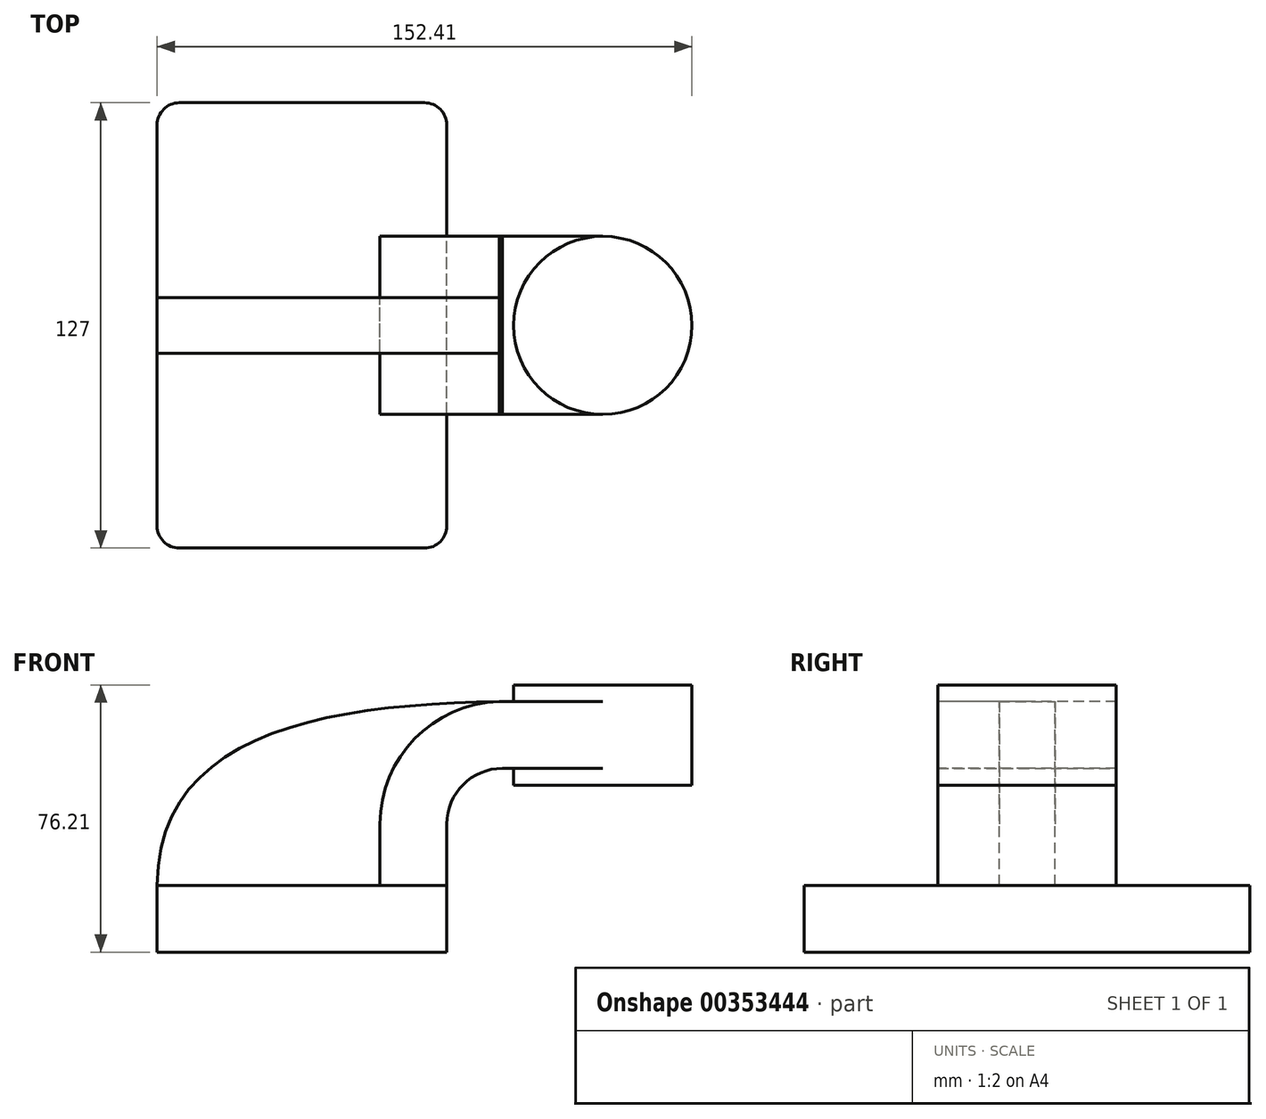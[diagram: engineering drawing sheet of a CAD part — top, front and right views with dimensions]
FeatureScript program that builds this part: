
annotation { "Feature Type Name" : "Feature", "Feature Type Description" : "" }
export const myFeature = defineFeature(function(context is Context, id is Id, definition is map)
    precondition{}
    {
        {
            var Q0;
            Q0=qCreatedBy(makeId("Front.planeOp"),FACE);
            var sketch = newSketch(context, id + "F0", { "sketchPlane" : qUnion([Q0])});
            skLineSegment(sketch, "E0.bottom", {"start": v(-41.28, -9.53) * mm, "end": v(41.28, -9.53) * mm});
            skLineSegment(sketch, "E0.top", {"start": v(-41.28, 9.53) * mm, "end": v(41.28, 9.53) * mm});
            skLineSegment(sketch, "E0.left", {"start": v(-41.28, -9.53) * mm, "end": v(-41.28, 9.53) * mm});
            skLineSegment(sketch, "E0.right", {"start": v(41.28, -9.53) * mm, "end": v(41.28, 9.53) * mm});
            skPoint(sketch, "E0.middle", {"position": v(0, 0) * mm});
            skLineSegment(sketch, "E1.bottom", {"start": v(60.33, 38.1) * mm, "end": v(111.12, 38.1) * mm});
            skLineSegment(sketch, "E1.top", {"start": v(60.33, 66.67) * mm, "end": v(111.12, 66.67) * mm});
            skLineSegment(sketch, "E1.left", {"start": v(60.33, 38.1) * mm, "end": v(60.33, 66.67) * mm});
            skLineSegment(sketch, "E1.right", {"start": v(111.12, 38.1) * mm, "end": v(111.12, 66.67) * mm});
            skPoint(sketch, "E1.middle", {"position": v(85.72, 52.39) * mm});
            skLineSegment(sketch, "E2", {"start": v(41.28, 9.53) * mm, "end": v(41.28, 27) * mm});
            skArc(sketch, "E3", {"start": v(41.27, 27) * mm, "mid": v(45.92, 38.23) * mm, "end": v(57.15, 42.88) * mm});
            skLineSegment(sketch, "E4", {"start": v(57.15, 42.88) * mm, "end": v(85.72, 42.88) * mm});
            skPoint(sketch, "E4.endSnap0", {"position": v(85.72, 38.1) * mm});
            skLineSegment(sketch, "E5.0", {"start": v(57.15, 61.93) * mm, "end": v(85.72, 61.93) * mm});
            skArc(sketch, "E5.1", {"start": v(22.23, 27) * mm, "mid": v(32.45, 51.7) * mm, "end": v(57.15, 61.93) * mm});
            skLineSegment(sketch, "E5.2", {"start": v(22.22, 9.53) * mm, "end": v(22.22, 27) * mm});
            skLineSegment(sketch, "E6", {"start": v(85.72, 38.1) * mm, "end": v(85.72, 66.67) * mm});
            skFitSpline(sketch, "E7", {"points": [v(-41.28, 9.53) * mm, v(57.15, 61.93) * mm], "startDerivative": vector(0.4, 131.51) * mm, "endDerivative": vector(149.24, 1.93) * mm});
            skSolve(sketch);
        }
        {
            var Q0;
            Q0=makeQuery(id+"F0.imprint","IMPRINT",FACE,{"disambiguationData":[TD([[makeQuery(id+"F0.imprint","IMPRINT",EDGE,{"derivedFrom":sQuery(id+"F0.wireOp",EDGE,"E0.bottom")}),1.0]])]});
            extrude(context, id + "F1", {"entities" : qUnion([Q0]), "endBound" : BoundingType.SYMMETRIC, "depth" : 127 * mm});
        }
        {
            var Q0;
            {var subQ1=sQuery(id+"F0.wireOp",EDGE,"E2");Q0=makeQuery(id+"F0.imprint","IMPRINT",FACE,{"disambiguationData":[TD([[makeQuery(id+"F0.imprint","IMPRINT",EDGE,{"derivedFrom":subQ1}),1.0]])]});}
            var Q1;
            {var subQ0=sQuery(id+"F0.wireOp",EDGE,"E4");var subQ1=sQuery(id+"F0.wireOp",EDGE,"E1.left");var subQ2=makeQuery(id+"F0.imprint","INTERSECT",VERTEX,{"derivedFrom":[subQ1,subQ0]});Q1=makeQuery(id+"F0.imprint","IMPRINT",FACE,{"disambiguationData":[TD([[makeQuery(id+"F0.imprint","IMPRINT",EDGE,{"disambiguationData":[TD([[subQ2,-1.0]])],"derivedFrom":subQ1}),-1.0]])]});}
            extrude(context, id + "F2", {"entities" : qUnion([Q0, Q1]), "endBound" : BoundingType.SYMMETRIC, "depth" : 50.8 * mm});
        }
        {
            var Q0;
            {var subQ3=sQuery(id+"F0.wireOp",EDGE,"E5.2");Q0=makeQuery(id+"F0.imprint","IMPRINT",FACE,{"disambiguationData":[TD([[makeQuery(id+"F0.imprint","IMPRINT",EDGE,{"derivedFrom":subQ3}),1.0]])]});}
            extrude(context, id + "F3", {"entities" : qUnion([Q0]), "endBound" : BoundingType.SYMMETRIC, "depth" : 15.88 * mm});
        }
        {
            var Q0;
            {var subQ4=sQuery(id+"F0.wireOp",EDGE,"E1.right");Q0=makeQuery(id+"F0.imprint","IMPRINT",FACE,{"disambiguationData":[TD([[makeQuery(id+"F0.imprint","IMPRINT",EDGE,{"derivedFrom":subQ4}),1.0]])]});}
            var Q1;
            Q1=sQuery(id+"F0.wireOp",EDGE,"E6");
            revolve(context, id + "F4", {"operationType" : NewBodyOperationType.ADD, "entities" : qUnion([Q0]), "axis" : qUnion([Q1]), "revolveType" : RevolveType.FULL});
        }
        {
            var Q0;
            Q0=makeQuery(id+"F1.opExtrude","CAP_EDGE",EDGE,{"disambiguationData":[OSD([sQuery(id+"F0.wireOp",EDGE,"E0.left")])],"isStart":false});
            var Q1;
            Q1=makeQuery(id+"F1.opExtrude","CAP_EDGE",EDGE,{"disambiguationData":[OSD([sQuery(id+"F0.wireOp",EDGE,"E0.right")])],"isStart":false});
            var Q2;
            Q2=makeQuery(id+"F1.opExtrude","CAP_EDGE",EDGE,{"disambiguationData":[OSD([sQuery(id+"F0.wireOp",EDGE,"E0.right")])],"isStart":true});
            var Q3;
            Q3=makeQuery(id+"F1.opExtrude","CAP_EDGE",EDGE,{"disambiguationData":[OSD([sQuery(id+"F0.wireOp",EDGE,"E0.left")])],"isStart":true});
            fillet(context, id + "F5", {"entities" : qUnion([Q0, Q1, Q2, Q3]), "radius" : 6.35 * mm, "tangentPropagation" : true, "allowEdgeOverflow" : false});
        }
    });
